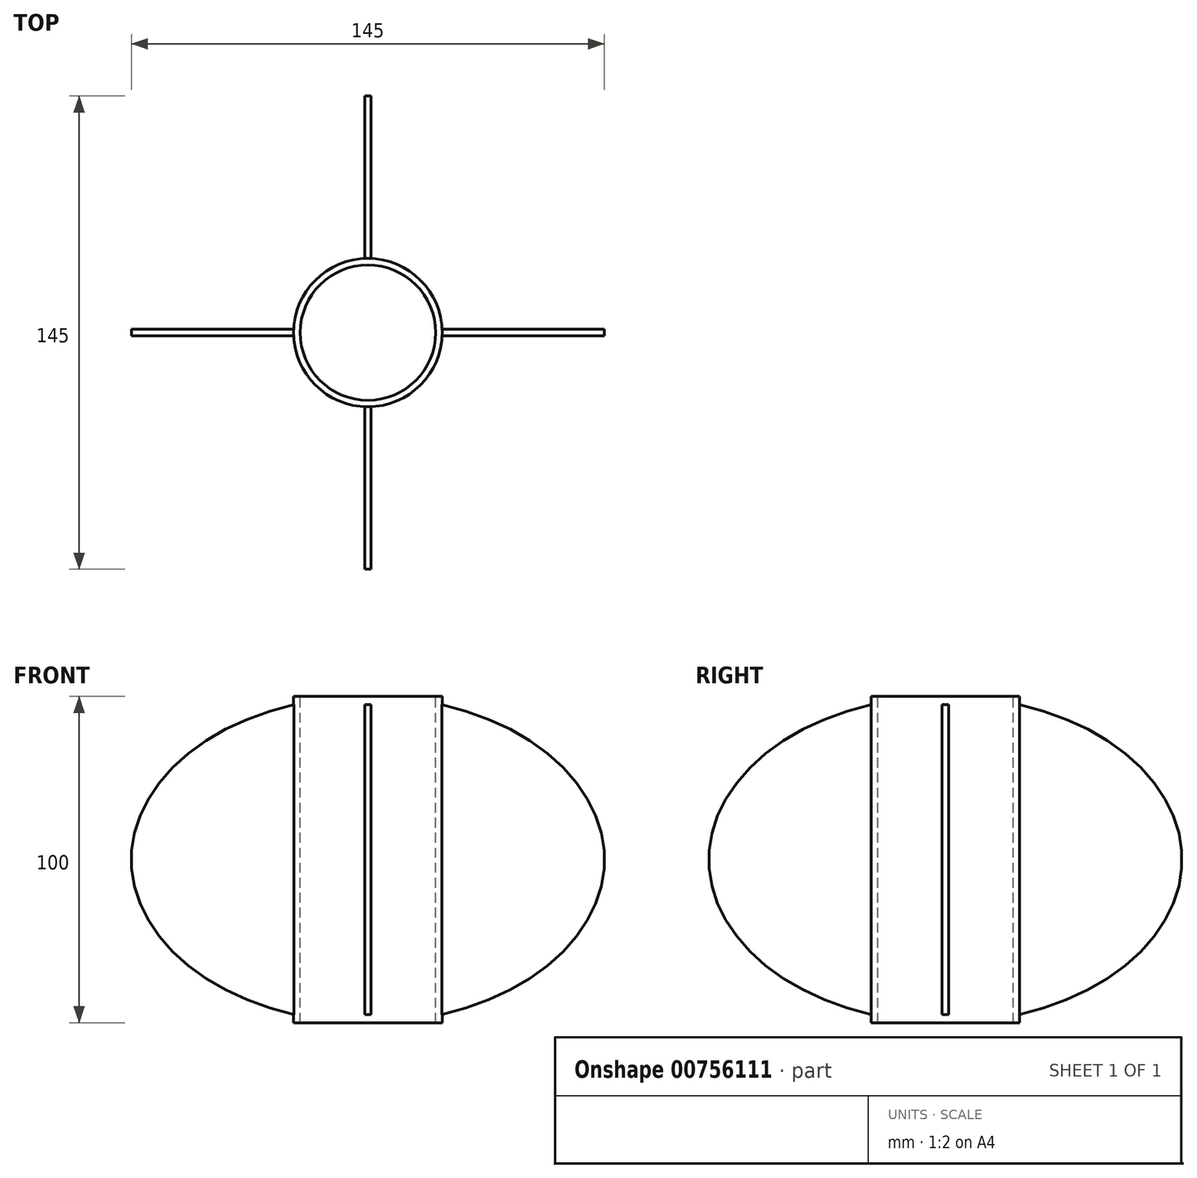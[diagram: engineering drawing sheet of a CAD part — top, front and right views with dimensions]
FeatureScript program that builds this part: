
annotation { "Feature Type Name" : "Feature", "Feature Type Description" : "" }
export const myFeature = defineFeature(function(context is Context, id is Id, definition is map)
    precondition{}
    {
        {
            assignVariable(context, id + "F0", {"name" : "finThickness", "anyValue" : 2});
        }
        {
            var Q0;
            Q0=qCreatedBy(makeId("Front.planeOp"),FACE);
            var sketch = newSketch(context, id + "F1", { "sketchPlane" : qUnion([Q0])});
            skEllipse(sketch, "E0", {"center": v(0, 0) * mm, "majorRadius": 72.5 * mm, "minorRadius": 50 * mm, "majorAxis": v(-1, 0)});
            skSolve(sketch);
        }
        {
            var Q0;
            Q0=qCreatedBy(makeId("Right.planeOp"),FACE);
            var sketch = newSketch(context, id + "F2", { "sketchPlane" : qUnion([Q0])});
            skEllipse(sketch, "E1", {"center": v(0, 0) * mm, "majorRadius": 72.5 * mm, "minorRadius": 50 * mm, "majorAxis": v(-1, 0)});
            skSolve(sketch);
        }
        {
            var Q0;
            Q0=qSketchRegion(id+"F1",true);
            extrude(context, id + "F3", {"entities" : qUnion([Q0]), "endBound" : BoundingType.SYMMETRIC, "depth" : (getVariable(context, 'finThickness')) * mm, "offsetDistance" : 25.4 * mm});
        }
        {
            var Q0;
            Q0=qSketchRegion(id+"F2",true);
            extrude(context, id + "F4", {"entities" : qUnion([Q0]), "operationType" : NewBodyOperationType.ADD, "endBound" : BoundingType.SYMMETRIC, "depth" : (getVariable(context, 'finThickness')) * mm, "offsetDistance" : 25.4 * mm});
        }
        {
            var Q0;
            Q0=qCreatedBy(makeId("Top.planeOp"),FACE);
            var sketch = newSketch(context, id + "F5", { "sketchPlane" : qUnion([Q0])});
            skCircle(sketch, "E2", {"center": v(0, 0) * mm, "radius": 22.75 * mm});
            skSolve(sketch);
        }
        {
            var Q0;
            Q0=qSketchRegion(id+"F5",true);
            extrude(context, id + "F6", {"entities" : qUnion([Q0]), "operationType" : NewBodyOperationType.ADD, "endBound" : BoundingType.SYMMETRIC, "depth" : 100 * mm, "offsetDistance" : 25.4 * mm});
        }
        {
            var Q0;
            Q0=makeQuery(id+"F6.opExtrude","CAP_FACE",FACE,{"disambiguationData":[OSD([sQuery(id+"F5.wireOp",EDGE,"E2")])],"isStart":false});
            var sketch = newSketch(context, id + "F7", { "sketchPlane" : qUnion([Q0])});
            skCircle(sketch, "E3", {"center": v(0, 0) * mm, "radius": 20.75 * mm});
            skSolve(sketch);
        }
        {
            var Q0;
            Q0=qSketchRegion(id+"F7",true);
            extrude(context, id + "F8", {"entities" : qUnion([Q0]), "operationType" : NewBodyOperationType.REMOVE, "endBound" : BoundingType.THROUGH_ALL, "oppositeDirection" : true, "depth" : 25.4 * mm, "offsetDistance" : 25.4 * mm});
        }
    });
